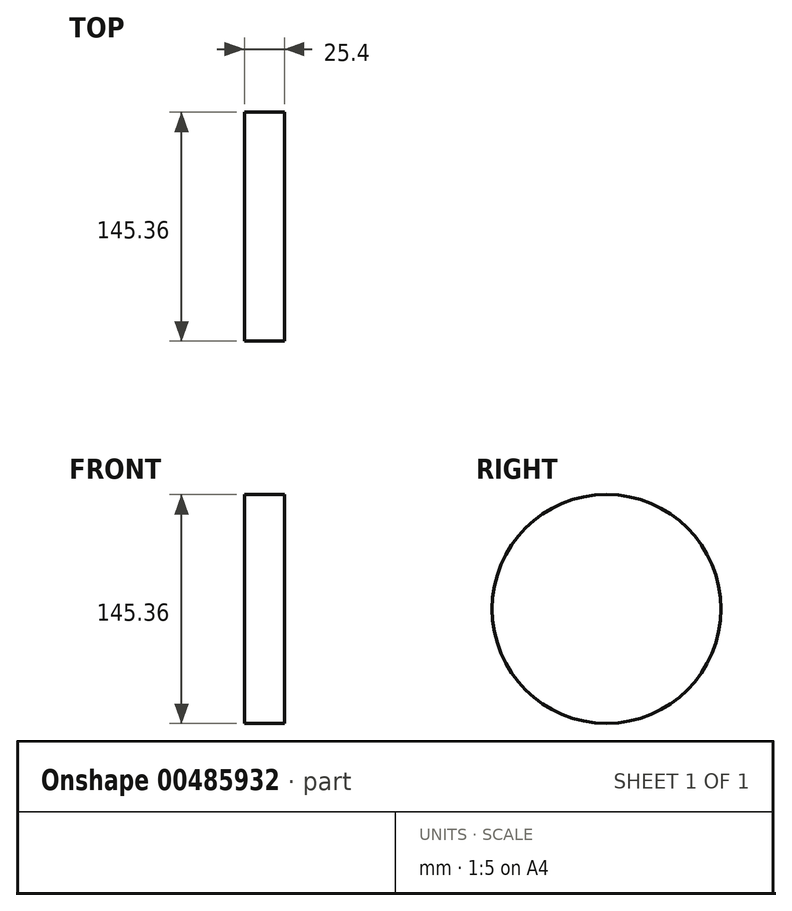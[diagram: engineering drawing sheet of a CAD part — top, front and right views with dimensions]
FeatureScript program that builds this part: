
annotation { "Feature Type Name" : "Feature", "Feature Type Description" : "" }
export const myFeature = defineFeature(function(context is Context, id is Id, definition is map)
    precondition{}
    {
        {
            var Q0;
            Q0=qCreatedBy(makeId("Right.planeOp"),FACE);
            var sketch = newSketch(context, id + "F0", { "sketchPlane" : qUnion([Q0])});
            skCircle(sketch, "E0", {"center": v(0, 0) * mm, "radius": 72.68 * mm});
            skSolve(sketch);
        }
        {
            var Q0;
            Q0 = qSketchRegion(id + "F0", true);
            extrude(context, id + "F1", {"entities" : qUnion([Q0]), "depth" : 25.4 * mm});
        }
    });
